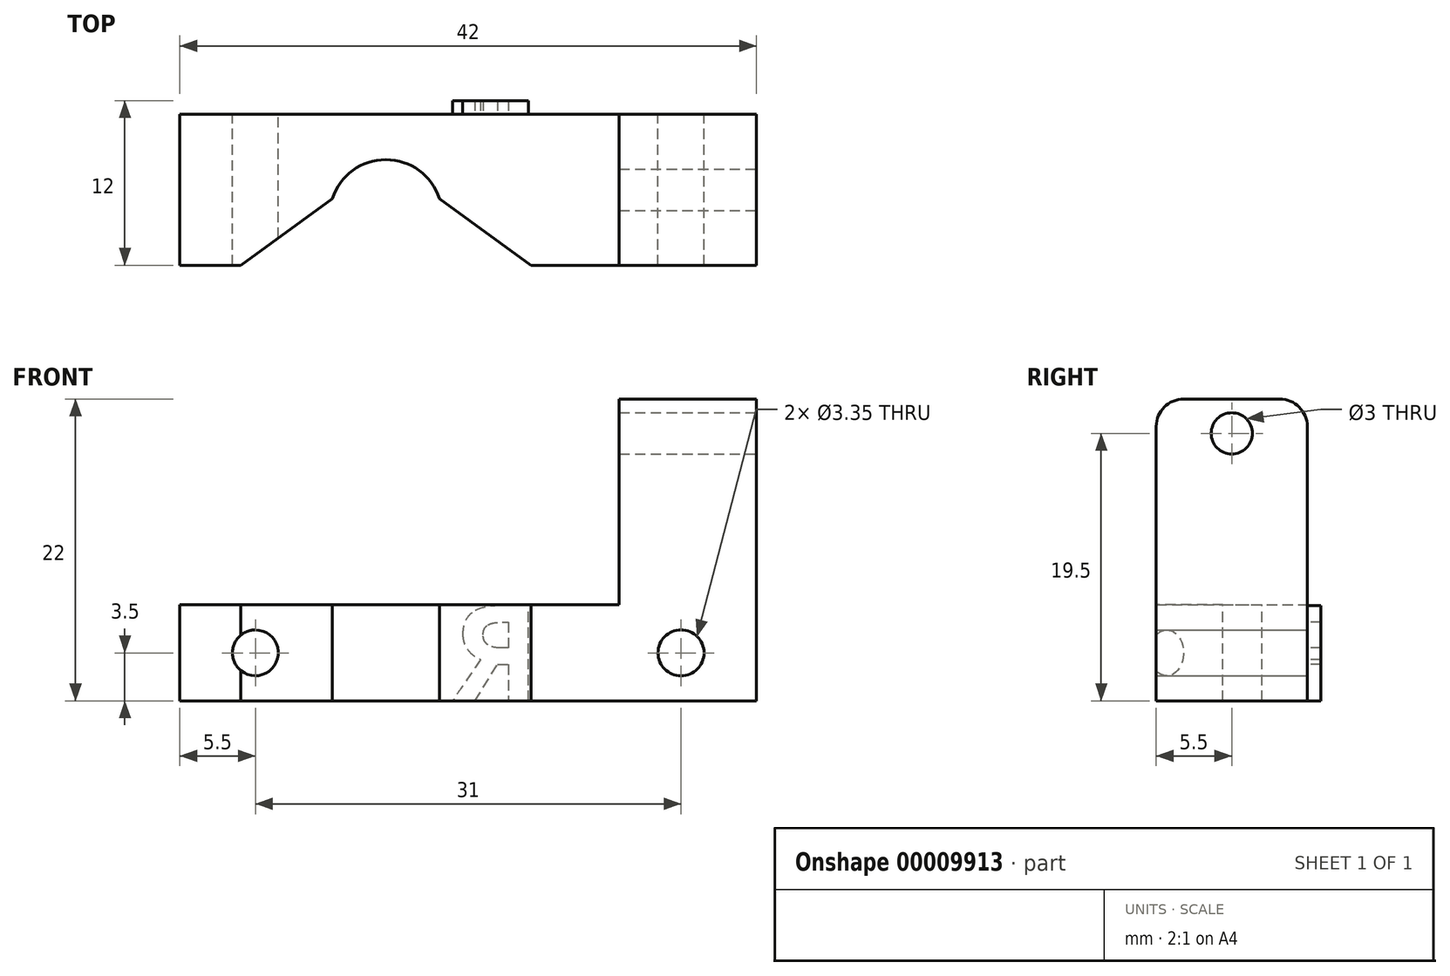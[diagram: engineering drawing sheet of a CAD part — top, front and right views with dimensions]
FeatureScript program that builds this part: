
annotation { "Feature Type Name" : "Feature", "Feature Type Description" : "" }
export const myFeature = defineFeature(function(context is Context, id is Id, definition is map)
    precondition{}
    {
        {
            assignVariable(context, id + "F0", {"name" : "rods", "anyValue" : 8});
        }
        {
            var Q0;
            Q0=qCreatedBy(makeId("Top.planeOp"),FACE);
            var sketch = newSketch(context, id + "F1", { "sketchPlane" : qUnion([Q0])});
            skLineSegment(sketch, "E0.bottom", {"start": v(0, 0) * mm, "end": v(42, 0) * mm});
            skLineSegment(sketch, "E0.top", {"start": v(0, 11) * mm, "end": v(42, 11) * mm});
            skLineSegment(sketch, "E0.left", {"start": v(0, 0) * mm, "end": v(0, 11) * mm});
            skLineSegment(sketch, "E0.right", {"start": v(42, 0) * mm, "end": v(42, 11) * mm});
            skSolve(sketch);
        }
        {
            var Q0;
            Q0 = qSketchRegion(id + "F1", true);
            extrude(context, id + "F2", {"entities" : qUnion([Q0]), "depth" : 7 * mm});
        }
        {
            var Q0;
            Q0=makeQuery(id+"F2.opExtrude","CAP_FACE",FACE,{"disambiguationData":[OSD([sQuery(id+"F1.wireOp",EDGE,"E0.bottom"),sQuery(id+"F1.wireOp",EDGE,"E0.top"),sQuery(id+"F1.wireOp",EDGE,"E0.left"),sQuery(id+"F1.wireOp",EDGE,"E0.right")])],"isStart":false});
            var sketch = newSketch(context, id + "F3", { "sketchPlane" : qUnion([Q0])});
            skCircle(sketch, "E1", {"center": v(15, 3.6) * mm, "radius": 4.1 * mm});
            skSolve(sketch);
        }
        {
            var Q0;
            Q0 = qSketchRegion(id + "F3", true);
            extrude(context, id + "F4", {"entities" : qUnion([Q0]), "operationType" : NewBodyOperationType.REMOVE, "oppositeDirection" : true, "depth" : 25 * mm});
        }
        {
            var Q0;
            Q0=makeQuery(id+"F4.boolean.opBoolean","INTERSECT",EDGE,{"disambiguationData":[OD(0.0)],"derivedFrom":[makeQuery(id+"F2.opExtrude","SWEPT_FACE",FACE,{"disambiguationData":[OSD([sQuery(id+"F1.wireOp",EDGE,"E0.bottom")])]}),makeQuery(id+"F4.opExtrude","SWEPT_FACE",FACE,{"disambiguationData":[OSD([sQuery(id+"F3.wireOp",EDGE,"E1")])]})]});
            var Q1;
            Q1=makeQuery(id+"F4.boolean.opBoolean","INTERSECT",EDGE,{"disambiguationData":[OD(1.0)],"derivedFrom":[makeQuery(id+"F2.opExtrude","SWEPT_FACE",FACE,{"disambiguationData":[OSD([sQuery(id+"F1.wireOp",EDGE,"E0.bottom")])]}),makeQuery(id+"F4.opExtrude","SWEPT_FACE",FACE,{"disambiguationData":[OSD([sQuery(id+"F3.wireOp",EDGE,"E1")])]})]});
            chamfer(context, id + "F5", {"entities" : qUnion([Q0, Q1]), "width" : (getVariable(context, 'rods') - 1) * mm, "tangentPropagation" : true});
        }
        {
            var Q0;
            Q0=makeQuery(id+"F2.opExtrude","SWEPT_FACE",FACE,{"disambiguationData":[OSD([sQuery(id+"F1.wireOp",EDGE,"E0.top")])]});
            var sketch = newSketch(context, id + "F6", { "sketchPlane" : qUnion([Q0])});
            skCircle(sketch, "E2", {"center": v(-5.5, 3.5) * mm, "radius": 1.68 * mm});
            skCircle(sketch, "E3", {"center": v(-36.5, 3.5) * mm, "radius": 1.68 * mm});
            skLineSegment(sketch, "E4", {"start": v(-5.5, 0) * mm, "end": v(-5.5, 7) * mm});
            skLineSegment(sketch, "E5", {"start": v(-5.5, 3.5) * mm, "end": v(0, 3.5) * mm});
            skLineSegment(sketch, "E6", {"start": v(-36.5, 3.5) * mm, "end": v(-42, 3.5) * mm});
            skSolve(sketch);
        }
        {
            var Q0;
            Q0 = qSketchRegion(id + "F6", true);
            extrude(context, id + "F7", {"entities" : qUnion([Q0]), "operationType" : NewBodyOperationType.REMOVE, "oppositeDirection" : true, "depth" : 25 * mm});
        }
        {
            var Q0;
            Q0=makeQuery(id+"F2.opExtrude","SWEPT_FACE",FACE,{"disambiguationData":[OSD([sQuery(id+"F1.wireOp",EDGE,"E0.top")])]});
            var sketch = newSketch(context, id + "F8", { "sketchPlane" : qUnion([Q0])});
            skText(sketch, "E7", { "text": "R", "fontName": "OpenSans-Bold.ttf"});
            const initialGuessF8  = {"E7": [-0.02627, 0, 1, 0, 0.007]};
            skSetInitialGuess(sketch, initialGuessF8);
            skSolve(sketch);
        }
        {
            var Q0;
            Q0 = qSketchRegion(id + "F8", true);
            extrude(context, id + "F9", {"entities" : qUnion([Q0]), "operationType" : NewBodyOperationType.ADD, "depth" : 1 * mm});
        }
        {
            var Q0;
            Q0=makeQuery(id+"F2.opExtrude","CAP_FACE",FACE,{"disambiguationData":[OSD([sQuery(id+"F1.wireOp",EDGE,"E0.bottom"),sQuery(id+"F1.wireOp",EDGE,"E0.top"),sQuery(id+"F1.wireOp",EDGE,"E0.left"),sQuery(id+"F1.wireOp",EDGE,"E0.right")])],"isStart":false});
            var sketch = newSketch(context, id + "F10", { "sketchPlane" : qUnion([Q0])});
            skLineSegment(sketch, "E8.bottom", {"start": v(42, 0) * mm, "end": v(32, 0) * mm});
            skLineSegment(sketch, "E8.top", {"start": v(42, 11) * mm, "end": v(32, 11) * mm});
            skLineSegment(sketch, "E8.left", {"start": v(42, 0) * mm, "end": v(42, 11) * mm});
            skLineSegment(sketch, "E8.right", {"start": v(32, 0) * mm, "end": v(32, 11) * mm});
            skSolve(sketch);
        }
        {
            var Q0;
            Q0 = qSketchRegion(id + "F10", true);
            extrude(context, id + "F11", {"entities" : qUnion([Q0]), "operationType" : NewBodyOperationType.ADD, "depth" : 15 * mm});
        }
        {
            var Q0;
            Q0=makeQuery(id+"FJdLS7F1L1csLPb_1.boolean.opBoolean","MERGE",FACE,{"derivedFrom":[makeQuery(id+"F11.boolean.opBoolean","MERGE",FACE,{"derivedFrom":[makeQuery(id+"F2.opExtrude","SWEPT_FACE",FACE,{"disambiguationData":[OSD([sQuery(id+"F1.wireOp",EDGE,"E0.right")])]}),makeQuery(id+"F11.opExtrude","SWEPT_FACE",FACE,{"disambiguationData":[OSD([sQuery(id+"F10.wireOp",EDGE,"E8.left")])]})]}),makeQuery(id+"FJdLS7F1L1csLPb_1.opExtrude","SWEPT_FACE",FACE,{"disambiguationData":[OSD([sQuery(id+"F4Ds6MLMi3WL0gL_1.wireOp",EDGE,"f6963c6d-1d98-4eef-b5cd-deae189cd3ae.left")])]})]});
            var sketch = newSketch(context, id + "F12", { "sketchPlane" : qUnion([Q0])});
            skCircle(sketch, "E9", {"center": v(5.5, 19.5) * mm, "radius": 1.5 * mm});
            skPoint(sketch, "E10", {"position": v(0, 19.5) * mm});
            skPoint(sketch, "E11", {"position": v(5.5, 0) * mm});
            skSolve(sketch);
        }
        {
            var Q0;
            Q0 = qSketchRegion(id + "F12", true);
            extrude(context, id + "F13", {"entities" : qUnion([Q0]), "operationType" : NewBodyOperationType.REMOVE, "oppositeDirection" : true, "depth" : 25 * mm});
        }
        {
            var Q0;
            Q0=makeQuery(id+"F11.opExtrude","CAP_EDGE",EDGE,{"disambiguationData":[OSD([sQuery(id+"F10.wireOp",EDGE,"E8.bottom")])],"isStart":false});
            var Q1;
            Q1=makeQuery(id+"F11.opExtrude","CAP_EDGE",EDGE,{"disambiguationData":[OSD([sQuery(id+"F10.wireOp",EDGE,"E8.top")])],"isStart":false});
            fillet(context, id + "F14", {"entities" : qUnion([Q0, Q1]), "radius" : 2 * mm, "tangentPropagation" : true, "allowEdgeOverflow" : false});
        }
    });
